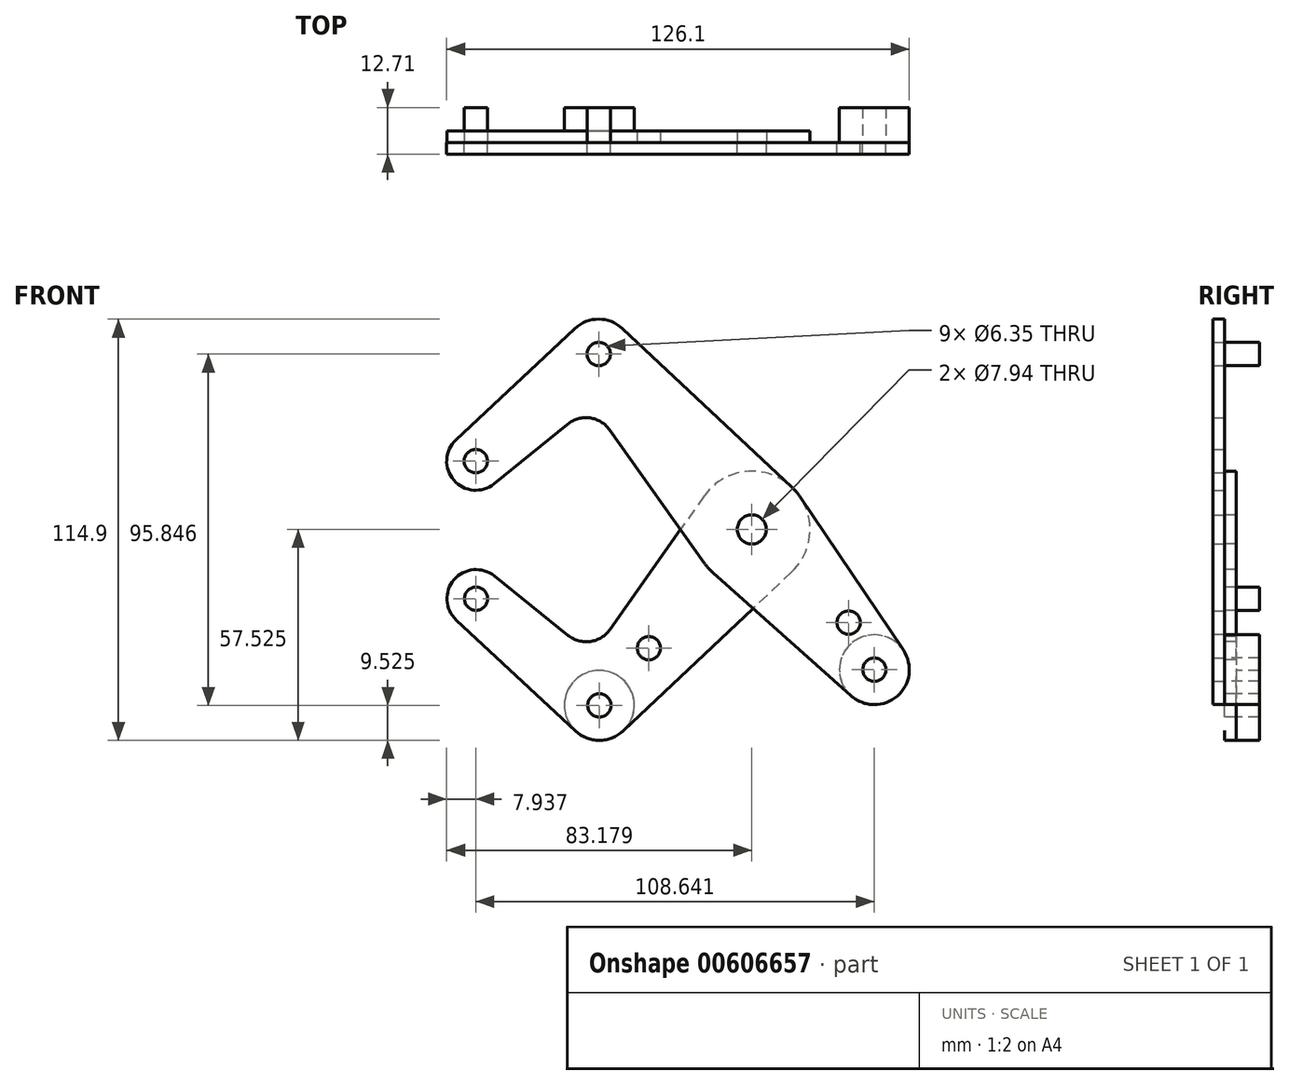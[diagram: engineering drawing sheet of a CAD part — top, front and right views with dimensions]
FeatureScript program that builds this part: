
annotation { "Feature Type Name" : "Feature", "Feature Type Description" : "" }
export const myFeature = defineFeature(function(context is Context, id is Id, definition is map)
    precondition{}
    {
        {
            var Q0;
            Q0=qCreatedBy(makeId("Front.planeOp"),FACE);
            var sketch = newSketch(context, id + "F0", { "sketchPlane" : qUnion([Q0])});
            skLineSegment(sketch, "E0", {"start": v(-13.85, 54.95) * mm, "end": v(69.65, -40.74) * mm, "construction": true});
            skCircle(sketch, "E1", {"center": v(27.9, 7.1) * mm, "radius": 3.18 * mm});
            skCircle(sketch, "E2", {"center": v(61.3, -31.17) * mm, "radius": 3.18 * mm});
            skCircle(sketch, "E3", {"center": v(-13.85, 54.95) * mm, "radius": 3.18 * mm});
            skCircle(sketch, "E4", {"center": v(-47.34, 25.73) * mm, "radius": 3.18 * mm});
            skLineSegment(sketch, "E5", {"start": v(-13.85, 54.95) * mm, "end": v(-47.34, 25.73) * mm, "construction": true});
            skCircle(sketch, "E6", {"center": v(61.3, -31.17) * mm, "radius": 9.53 * mm});
            skCircle(sketch, "E7", {"center": v(-47.34, 25.73) * mm, "radius": 7.94 * mm});
            skCircle(sketch, "E8", {"center": v(-13.85, 54.95) * mm, "radius": 9.53 * mm});
            skLineSegment(sketch, "E9", {"start": v(-52.77, 31.52) * mm, "end": v(-20.37, 61.9) * mm});
            skLineSegment(sketch, "E10", {"start": v(-42.34, 19.56) * mm, "end": v(-22.31, 35.82) * mm});
            skCircle(sketch, "E11", {"center": v(27.9, 7.1) * mm, "radius": 15.88 * mm});
            skLineSegment(sketch, "E12", {"start": v(-7.34, 61.9) * mm, "end": v(38.76, 18.69) * mm});
            skLineSegment(sketch, "E13", {"start": v(-10.84, 34.25) * mm, "end": v(14.95, -2.08) * mm});
            skLineSegment(sketch, "E14", {"start": v(17.34, -4.75) * mm, "end": v(54.96, -38.28) * mm});
            skLineSegment(sketch, "E15", {"start": v(41.07, 15.96) * mm, "end": v(69.2, -25.86) * mm});
            skArc(sketch, "E16.filletArc", {"start": v(-10.84, 34.25) * mm, "mid": v(-16.23, 37.52) * mm, "end": v(-22.31, 35.82) * mm});
            skLineSegment(sketch, "E17", {"start": v(27.9, 7.1) * mm, "end": v(-13.67, -40.9) * mm, "construction": true});
            skLineSegment(sketch, "E18", {"start": v(-13.67, -40.9) * mm, "end": v(-47.27, -11.8) * mm, "construction": true});
            skCircle(sketch, "E19", {"center": v(-47.27, -11.8) * mm, "radius": 3.18 * mm});
            skCircle(sketch, "E20", {"center": v(-13.67, -40.9) * mm, "radius": 3.18 * mm});
            skCircle(sketch, "E21", {"center": v(-47.27, -11.8) * mm, "radius": 7.94 * mm});
            skCircle(sketch, "E22", {"center": v(-13.67, -40.9) * mm, "radius": 9.53 * mm});
            skLineSegment(sketch, "E23", {"start": v(-42.3, -5.61) * mm, "end": v(-22.2, -21.8) * mm});
            skLineSegment(sketch, "E24", {"start": v(-52.68, -17.6) * mm, "end": v(-20.16, -47.87) * mm});
            skLineSegment(sketch, "E25", {"start": v(14.92, 16.25) * mm, "end": v(-10.74, -20.18) * mm});
            skLineSegment(sketch, "E26", {"start": v(38.8, -4.44) * mm, "end": v(-7.13, -47.82) * mm});
            skArc(sketch, "E27.filletArc", {"start": v(-22.2, -21.8) * mm, "mid": v(-16.12, -23.47) * mm, "end": v(-10.74, -20.18) * mm});
            skCircle(sketch, "E28", {"center": v(-0.16, -25.3) * mm, "radius": 3.18 * mm});
            skCircle(sketch, "E29", {"center": v(54.3, -18.32) * mm, "radius": 3.18 * mm});
            skLineSegment(sketch, "E30", {"start": v(54.3, -18.32) * mm, "end": v(51.9, -20.4) * mm, "construction": true});
            skCircle(sketch, "E31", {"center": v(27.9, 7.1) * mm, "radius": 3.97 * mm});
            skSolve(sketch);
        }
        {
            var Q0;
            {var subQ6=sQuery(id+"F0.wireOp",EDGE,"E9");Q0=makeQuery(id+"F0.imprint","IMPRINT",FACE,{"disambiguationData":[TD([[makeQuery(id+"F0.imprint","IMPRINT",EDGE,{"derivedFrom":subQ6}),-1.0]])]});}
            var Q1;
            Q1=makeQuery(id+"F0.imprint","IMPRINT",FACE,{"disambiguationData":[TD([[makeQuery(id+"F0.imprint","IMPRINT",EDGE,{"derivedFrom":sQuery(id+"F0.wireOp",EDGE,"E4")}),-1.0]])]});
            var Q2;
            Q2=makeQuery(id+"F0.imprint","IMPRINT",FACE,{"disambiguationData":[TD([[makeQuery(id+"F0.imprint","IMPRINT",EDGE,{"derivedFrom":sQuery(id+"F0.wireOp",EDGE,"E3")}),-1.0]])]});
            var Q3;
            Q3=makeQuery(id+"F0.imprint","IMPRINT",FACE,{"disambiguationData":[TD([[makeQuery(id+"F0.imprint","IMPRINT",EDGE,{"derivedFrom":sQuery(id+"F0.wireOp",EDGE,"E31")}),-1.0]])]});
            var Q4;
            {var subQ0=sQuery(id+"F0.wireOp",EDGE,"E15");Q4=makeQuery(id+"F0.imprint","IMPRINT",FACE,{"disambiguationData":[TD([[makeQuery(id+"F0.imprint","IMPRINT",EDGE,{"derivedFrom":subQ0}),-1.0]])]});}
            var Q5;
            Q5=makeQuery(id+"F0.imprint","IMPRINT",FACE,{"disambiguationData":[TD([[makeQuery(id+"F0.imprint","IMPRINT",EDGE,{"derivedFrom":sQuery(id+"F0.wireOp",EDGE,"E2")}),-1.0]])]});
            var Q6;
            {var subQ0=sQuery(id+"F0.wireOp",EDGE,"E13");var subQ1=sQuery(id+"F0.wireOp",EDGE,"E11");var subQ2=makeQuery(id+"F0.imprint","INTERSECT",VERTEX,{"derivedFrom":[subQ1,subQ0]});Q6=makeQuery(id+"F0.imprint","IMPRINT",FACE,{"disambiguationData":[TD([[makeQuery(id+"F0.imprint","IMPRINT",EDGE,{"disambiguationData":[TD([[subQ2,1.0]])],"derivedFrom":subQ1}),-1.0]])]});}
            var Q7;
            {var subQ0=sQuery(id+"F0.wireOp",EDGE,"E14");var subQ1=sQuery(id+"F0.wireOp",EDGE,"E11");var subQ2=makeQuery(id+"F0.imprint","INTERSECT",VERTEX,{"derivedFrom":[subQ1,subQ0]});Q7=makeQuery(id+"F0.imprint","IMPRINT",FACE,{"disambiguationData":[TD([[makeQuery(id+"F0.imprint","IMPRINT",EDGE,{"disambiguationData":[TD([[subQ2,-1.0]])],"derivedFrom":subQ1}),-1.0]])]});}
            extrude(context, id + "F1", {"entities" : qUnion([Q0, Q1, Q2, Q3, Q4, Q5, Q6, Q7]), "depth" : 3.17 * mm, "offsetDistance" : 25.4 * mm});
        }
        {
            var Q0;
            {var subQ13=sQuery(id+"F0.wireOp",EDGE,"E23");Q0=makeQuery(id+"F0.imprint","IMPRINT",FACE,{"disambiguationData":[TD([[makeQuery(id+"F0.imprint","IMPRINT",EDGE,{"derivedFrom":subQ13}),-1.0]])]});}
            var Q1;
            Q1=makeQuery(id+"F0.imprint","IMPRINT",FACE,{"disambiguationData":[TD([[makeQuery(id+"F0.imprint","IMPRINT",EDGE,{"derivedFrom":sQuery(id+"F0.wireOp",EDGE,"E31")}),-1.0]])]});
            var Q2;
            {var subQ0=sQuery(id+"F0.wireOp",EDGE,"E14");var subQ1=sQuery(id+"F0.wireOp",EDGE,"E11");var subQ2=makeQuery(id+"F0.imprint","INTERSECT",VERTEX,{"derivedFrom":[subQ1,subQ0]});Q2=makeQuery(id+"F0.imprint","IMPRINT",FACE,{"disambiguationData":[TD([[makeQuery(id+"F0.imprint","IMPRINT",EDGE,{"disambiguationData":[TD([[subQ2,-1.0]])],"derivedFrom":subQ1}),-1.0]])]});}
            var Q3;
            Q3=makeQuery(id+"F0.imprint","IMPRINT",FACE,{"disambiguationData":[TD([[makeQuery(id+"F0.imprint","IMPRINT",EDGE,{"derivedFrom":sQuery(id+"F0.wireOp",EDGE,"E20")}),-1.0]])]});
            var Q4;
            Q4=makeQuery(id+"F0.imprint","IMPRINT",FACE,{"disambiguationData":[TD([[makeQuery(id+"F0.imprint","IMPRINT",EDGE,{"derivedFrom":sQuery(id+"F0.wireOp",EDGE,"E19")}),-1.0]])]});
            var Q5;
            {var subQ0=sQuery(id+"F0.wireOp",EDGE,"E13");var subQ1=sQuery(id+"F0.wireOp",EDGE,"E11");var subQ2=makeQuery(id+"F0.imprint","INTERSECT",VERTEX,{"derivedFrom":[subQ1,subQ0]});Q5=makeQuery(id+"F0.imprint","IMPRINT",FACE,{"disambiguationData":[TD([[makeQuery(id+"F0.imprint","IMPRINT",EDGE,{"disambiguationData":[TD([[subQ2,1.0]])],"derivedFrom":subQ1}),-1.0]])]});}
            extrude(context, id + "F2", {"entities" : qUnion([Q0, Q1, Q2, Q3, Q4, Q5]), "oppositeDirection" : true, "depth" : 3.17 * mm, "offsetDistance" : 25.4 * mm});
        }
        {
            var Q0;
            Q0=qCreatedBy(makeId("Front.planeOp"),FACE);
            cPlane(context, id + "F3", {"entities" : qUnion([Q0]), "cplaneType" : CPlaneType.OFFSET, "offset" : 9.52 * mm, "oppositeDirection" : true, "width" : 152.4 * mm, "height" : 152.4 * mm});
        }
        {
            var Q0;
            Q0=makeQuery(id+"F0.imprint","IMPRINT",FACE,{"disambiguationData":[TD([[makeQuery(id+"F0.imprint","IMPRINT",EDGE,{"derivedFrom":sQuery(id+"F0.wireOp",EDGE,"E2")}),-1.0]])]});
            var Q1;
            Q1=makeQuery(id+"F0.imprint","IMPRINT",FACE,{"disambiguationData":[TD([[makeQuery(id+"F0.imprint","IMPRINT",EDGE,{"derivedFrom":sQuery(id+"F0.wireOp",EDGE,"E3")}),1.0]])]});
            var Q2;
            Q2=makeQuery(id+"F0.imprint","IMPRINT",FACE,{"disambiguationData":[TD([[makeQuery(id+"F0.imprint","IMPRINT",EDGE,{"derivedFrom":sQuery(id+"F0.wireOp",EDGE,"E20")}),-1.0]])]});
            var Q3;
            Q3=makeQuery(id+"F0.imprint","IMPRINT",FACE,{"disambiguationData":[TD([[makeQuery(id+"F0.imprint","IMPRINT",EDGE,{"derivedFrom":sQuery(id+"F0.wireOp",EDGE,"E19")}),1.0]])]});
            var Q4;
            Q4=qCreatedBy(id+"F3.planeOp",FACE);
            extrude(context, id + "F4", {"entities" : qUnion([Q0, Q1, Q2, Q3]), "endBound" : BoundingType.UP_TO_SURFACE, "oppositeDirection" : true, "depth" : 25.4 * mm, "endBoundEntityFace" : qUnion([Q4]), "offsetDistance" : 25.4 * mm});
        }
        {
            var Q0;
            Q0=makeQuery(id+"F1.opExtrude","SWEPT_BODY",BODY,{"disambiguationData":[OSD([sQuery(id+"F0.wireOp",EDGE,"E2"),sQuery(id+"F0.wireOp",EDGE,"E3"),sQuery(id+"F0.wireOp",EDGE,"E4"),sQuery(id+"F0.wireOp",EDGE,"E6"),sQuery(id+"F0.wireOp",EDGE,"E7"),sQuery(id+"F0.wireOp",EDGE,"E8"),sQuery(id+"F0.wireOp",EDGE,"E9"),sQuery(id+"F0.wireOp",EDGE,"E10"),sQuery(id+"F0.wireOp",EDGE,"E11"),sQuery(id+"F0.wireOp",EDGE,"E12"),sQuery(id+"F0.wireOp",EDGE,"E13"),sQuery(id+"F0.wireOp",EDGE,"E14"),sQuery(id+"F0.wireOp",EDGE,"E15"),sQuery(id+"F0.wireOp",EDGE,"E16.filletArc"),sQuery(id+"F0.wireOp",EDGE,"E29"),sQuery(id+"F0.wireOp",EDGE,"E31")])]});
            var Q1;
            Q1=makeQuery(id+"F2.opExtrude","SWEPT_BODY",BODY,{"disambiguationData":[OSD([sQuery(id+"F0.wireOp",EDGE,"E11"),sQuery(id+"F0.wireOp",EDGE,"E19"),sQuery(id+"F0.wireOp",EDGE,"E20"),sQuery(id+"F0.wireOp",EDGE,"E21"),sQuery(id+"F0.wireOp",EDGE,"E22"),sQuery(id+"F0.wireOp",EDGE,"E23"),sQuery(id+"F0.wireOp",EDGE,"E24"),sQuery(id+"F0.wireOp",EDGE,"E25"),sQuery(id+"F0.wireOp",EDGE,"E26"),sQuery(id+"F0.wireOp",EDGE,"E27.filletArc"),sQuery(id+"F0.wireOp",EDGE,"E28"),sQuery(id+"F0.wireOp",EDGE,"E31")])]});
            var Q2;
            Q2=makeQuery(id+"F4.opExtrude","SWEPT_BODY",BODY,{"disambiguationData":[OSD([sQuery(id+"F0.wireOp",EDGE,"E3")])]});
            var Q3;
            Q3=makeQuery(id+"F4.opExtrude","SWEPT_BODY",BODY,{"disambiguationData":[OSD([sQuery(id+"F0.wireOp",EDGE,"E20"),sQuery(id+"F0.wireOp",EDGE,"E22")])]});
            var Q4;
            Q4=makeQuery(id+"F4.opExtrude","SWEPT_BODY",BODY,{"disambiguationData":[OSD([sQuery(id+"F0.wireOp",EDGE,"E2"),sQuery(id+"F0.wireOp",EDGE,"E6")])]});
            booleanBodies(context, id + "F5", {"operationType" : BooleanOperationType.SUBTRACTION, "tools" : qUnion([Q0, Q1]), "targets" : qUnion([Q2, Q3, Q4]), "keepTools" : true});
        }
    });
